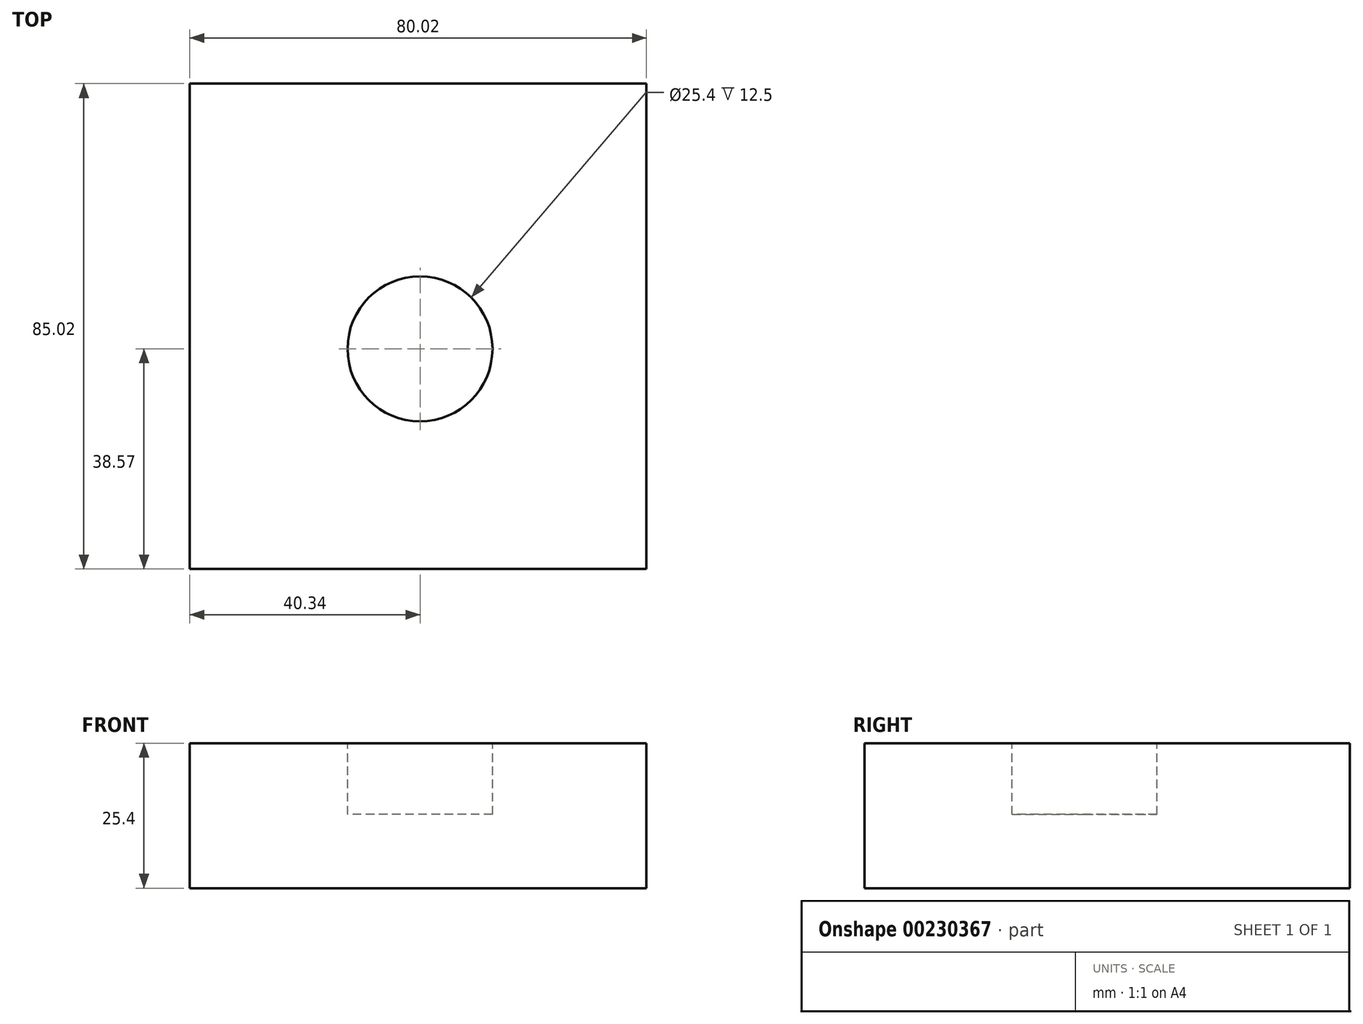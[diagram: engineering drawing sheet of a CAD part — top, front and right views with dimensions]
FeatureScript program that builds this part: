
annotation { "Feature Type Name" : "Feature", "Feature Type Description" : "" }
export const myFeature = defineFeature(function(context is Context, id is Id, definition is map)
    precondition{}
    {
        {
            var Q0;
            Q0=qCreatedBy(makeId("Top.planeOp"),FACE);
            var sketch = newSketch(context, id + "F0", { "sketchPlane" : qUnion([Q0])});
            skLineSegment(sketch, "E0.bottom", {"start": v(-40.34, 46.45) * mm, "end": v(39.68, 46.45) * mm});
            skLineSegment(sketch, "E0.top", {"start": v(-40.34, -38.57) * mm, "end": v(39.68, -38.57) * mm});
            skLineSegment(sketch, "E0.left", {"start": v(-40.34, 46.45) * mm, "end": v(-40.34, -38.57) * mm});
            skLineSegment(sketch, "E0.right", {"start": v(39.68, 46.45) * mm, "end": v(39.68, -38.57) * mm});
            skSolve(sketch);
        }
        {
            var Q0;
            Q0=makeQuery(id+"F0.imprint","IMPRINT",FACE,{"disambiguationData":[TD([[makeQuery(id+"F0.imprint","IMPRINT",EDGE,{"derivedFrom":sQuery(id+"F0.wireOp",EDGE,"E0.bottom")}),-1.0]])]});
            extrude(context, id + "F1", {"entities" : qUnion([Q0]), "depth" : 25.4 * mm});
        }
        {
            var Q0;
            Q0=makeQuery(id+"F1.opExtrude","CAP_FACE",FACE,{"disambiguationData":[OSD([sQuery(id+"F0.wireOp",EDGE,"E0.bottom"),sQuery(id+"F0.wireOp",EDGE,"E0.top"),sQuery(id+"F0.wireOp",EDGE,"E0.left"),sQuery(id+"F0.wireOp",EDGE,"E0.right")])],"isStart":false});
            var sketch = newSketch(context, id + "F3", { "sketchPlane" : qUnion([Q0])});
            skCircle(sketch, "E1", {"center": v(0, 0) * mm, "radius": 12.7 * mm});
            skSolve(sketch);
        }
        {
            var Q0;
            Q0 = qSketchRegion(id + "F3", true);
            extrude(context, id + "F2", {"entities" : qUnion([Q0]), "operationType" : NewBodyOperationType.REMOVE, "endBound" : BoundingType.SYMMETRIC, "oppositeDirection" : true, "depth" : 25 * mm});
        }
    });
